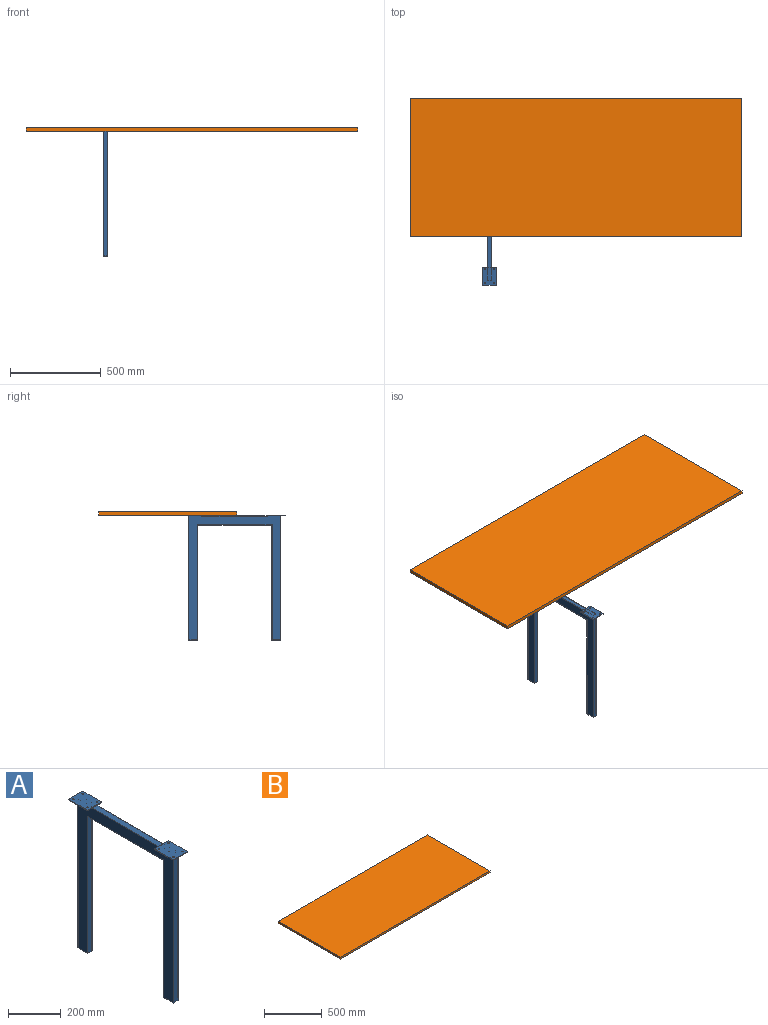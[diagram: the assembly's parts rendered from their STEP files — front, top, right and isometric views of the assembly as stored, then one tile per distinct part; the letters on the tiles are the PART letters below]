
ASSEMBLY  parts=2 mates=1
PART A: 44 faces, bbox 76.2x560.4x689 mm
  f0: plane 407.99x25.4mm, normal (0,0,-1), area 10362.9mm2, adj f22,f24,f26,f28
  f1: plane 76.2x3.18mm, normal (0,-1,0), area 241.9mm2, adj f2,f4,f5,f6
  f2: plane 101.6x3.18mm, normal (1,0,0), area 322.6mm2, adj f1,f3,f5,f6
  f3: plane 76.2x3.18mm, normal (0,1,0), area 241.9mm2, adj f2,f4,f5,f6,f21
  f4: plane 101.6x3.18mm, normal (-1,0,0), area 322.6mm2, adj f1,f3,f5,f6
  f5: plane 101.6x76.2mm, normal (0,0,-1), area 5679.8mm2, adj f1,f2,f3,f4,f7,f8,f9,f10
  f6: plane 101.6x76.2mm, normal (0,0,1), area 7615.2mm2, adj f1,f2,f3,f4,f7,f8,f9,f10
  f7: cylinder r=3.17mm len=6.35mm, axis (0,0,1), area 63.3mm2, adj f5,f6
  f8: cylinder r=3.17mm len=6.35mm, axis (0,0,1), area 63.3mm2, adj f5,f6
  f9: cylinder r=3.17mm len=6.35mm, axis (0,0,1), area 63.3mm2, adj f5,f6
  f10: cylinder r=3.17mm len=6.35mm, axis (0,0,1), area 63.3mm2, adj f5,f6
  f11: plane 76.2x3.18mm, normal (0,-1,0), area 241.9mm2, adj f12,f14,f15,f16,f21
  f12: plane 101.6x3.18mm, normal (1,0,0), area 322.6mm2, adj f11,f13,f15,f16
  f13: plane 76.2x3.18mm, normal (0,1,0), area 241.9mm2, adj f12,f14,f15,f16
  f14: plane 101.6x3.18mm, normal (-1,0,0), area 322.6mm2, adj f11,f13,f15,f16
  f15: plane 101.6x76.2mm, normal (0,0,-1), area 5679.8mm2, adj f11,f12,f13,f14,f17,f18,f19,f20
  f16: plane 101.6x76.2mm, normal (0,0,1), area 7615.2mm2, adj f11,f12,f13,f14,f17,f18,f19,f20
  f17: cylinder r=3.17mm len=6.35mm, axis (0,0,1), area 63.3mm2, adj f15,f16
  f18: cylinder r=3.17mm len=6.35mm, axis (0,0,1), area 63.3mm2, adj f15,f16
  f19: cylinder r=3.17mm len=6.35mm, axis (0,0,1), area 63.3mm2, adj f15,f16
  f20: cylinder r=3.17mm len=6.35mm, axis (0,0,1), area 63.3mm2, adj f15,f16
  f21: plane 357.19x25.4mm, normal (0,0,1), area 9072.6mm2, adj f3,f11,f22,f24
  f22: plane 685.8x509.59mm, normal (1,0,0), area 90403mm2, adj f0,f5,f15,f21,f23,f25,f26,f27
  f23: plane 685.8x25.4mm, normal (0,-1,0), area 17419.3mm2, adj f5,f22,f24,f27
  f24: plane 685.8x509.59mm, normal (-1,0,0), area 90403mm2, adj f0,f5,f15,f21,f23,f25,f26,f27
  f25: plane 685.8x25.4mm, normal (0,1,0), area 17419.3mm2, adj f15,f22,f24,f29
  f26: plane 635x25.4mm, normal (0,1,0), area 16129mm2, adj f0,f22,f24,f27
  f27: plane 50.8x25.4mm, normal (0,0,-1), area 1290.3mm2, adj f22,f23,f24,f26
  f28: plane 635x25.4mm, normal (0,-1,0), area 16129mm2, adj f0,f22,f24,f29
  f29: plane 50.8x25.4mm, normal (0,0,-1), area 1290.3mm2, adj f22,f24,f25,f28
  f30: plane 413.07x20.32mm, normal (0,0,1), area 8393.5mm2, adj f36,f38,f40,f42
  f31: plane 20.32x3.18mm, normal (0,-1,0), area 64.5mm2, adj f32,f35,f36,f38
  f32: plane 71.12x20.32mm, normal (0,0,-1), area 1445.2mm2, adj f31,f36,f37,f38
  f33: plane 20.32x3.18mm, normal (0,1,0), area 64.5mm2, adj f34,f35,f36,f38
  f34: plane 71.12x20.32mm, normal (0,0,-1), area 1445.2mm2, adj f33,f36,f38,f39
  f35: plane 362.27x20.32mm, normal (0,0,-1), area 7361.3mm2, adj f31,f33,f36,f38
  f36: plane 683.9x504.51mm, normal (-1,0,0), area 81582.1mm2, adj f30,f31,f32,f33,f34,f35,f37,f39
  f37: plane 683.9x20.32mm, normal (0,1,0), area 13896.7mm2, adj f32,f36,f38,f41
  f38: plane 683.9x504.51mm, normal (1,0,0), area 81582.1mm2, adj f30,f31,f32,f33,f34,f35,f37,f39
  f39: plane 683.9x20.32mm, normal (0,-1,0), area 13896.7mm2, adj f34,f36,f38,f43
  f40: plane 635x20.32mm, normal (0,-1,0), area 12903.2mm2, adj f30,f36,f38,f41
  f41: plane 45.72x20.32mm, normal (0,0,1), area 929mm2, adj f36,f37,f38,f40
  f42: plane 635x20.32mm, normal (0,1,0), area 12903.2mm2, adj f30,f36,f38,f43
  f43: plane 45.72x20.32mm, normal (0,0,1), area 929mm2, adj f36,f38,f39,f42
PART B: 6 faces, bbox 1828.8x762x19.1 mm
  f0: plane 1828.8x19.05mm, normal (0,1,0), area 34838.6mm2, adj f1,f3,f4,f5
  f1: plane 762x19.05mm, normal (-1,0,0), area 14516.1mm2, adj f0,f2,f4,f5
  f2: plane 1828.8x19.05mm, normal (0,-1,0), area 34838.6mm2, adj f1,f3,f4,f5
  f3: plane 762x19.05mm, normal (1,0,0), area 14516.1mm2, adj f0,f2,f4,f5
  f4: plane 1828.8x762mm, normal (0,0,-1), area 1393545.6mm2, adj f0,f1,f2,f3
  f5: plane 1828.8x762mm, normal (0,0,1), area 1393545.6mm2, adj f0,f1,f2,f3
PLACE A t=(-477.27,-369.9,-9.52)mm
PLACE B t=(0,-381,9.52)mm
MATE planar A.f6 <-> B.f4  axis (0,0,1) through (-477.27,-599.29,-9.52)mm
